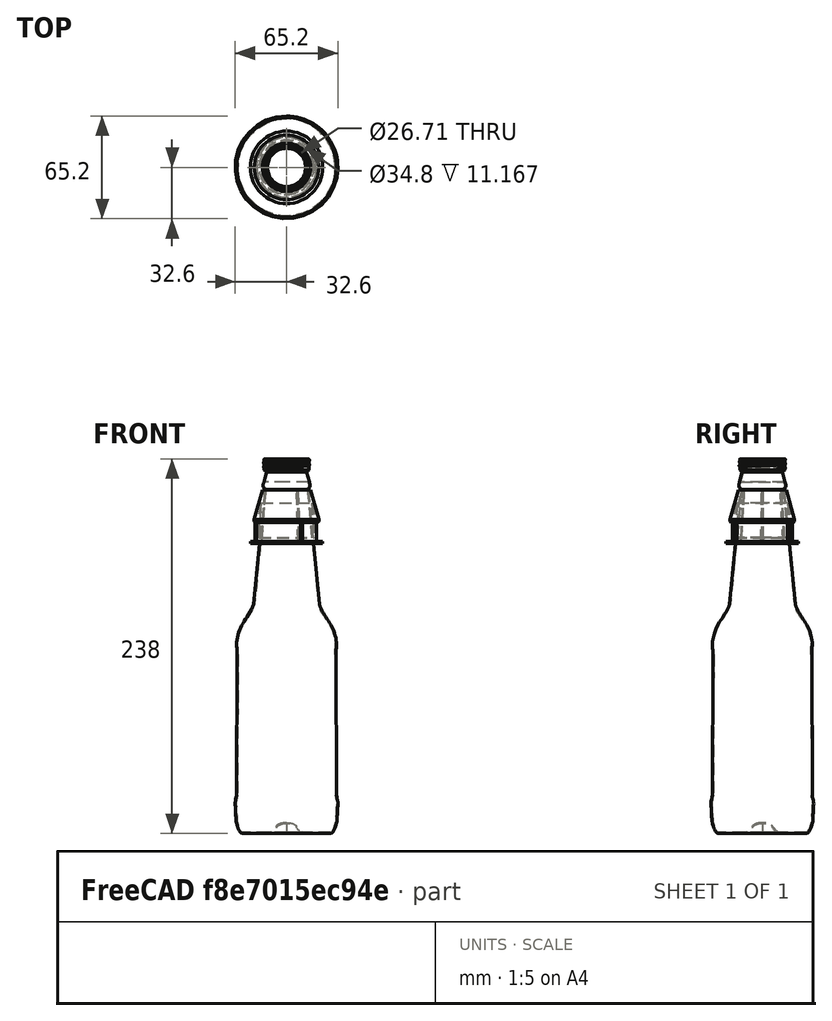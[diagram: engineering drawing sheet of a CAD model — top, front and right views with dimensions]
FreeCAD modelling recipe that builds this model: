
FCSTD DOCUMENT  (FreeCAD 1.0R39319 (Git))
Label: beer_bottle_mount
License: CERN Open Hardware Licence permissive
LicenseURL: https://cern-ohl.web.cern.ch/
objects: Sketcher::SketchObject×3, PartDesign::Pad×2, PartDesign::PolarPattern×2, PartDesign::Revolution×1, Part::Feature×1, Part::Scale×1, Part::FeaturePython×1, PartDesign::Body×1
note: 23 computed .brp shape members not serialized (recipe doc carries the construction recipe); baked Part::Feature solids carry a one-line shape summary decoded from their .brp

FEATURE [Sketcher::SketchObject] Sketch
  ArcFitTolerance = 1e-06
  AttachmentSupport = -> [XZ_Plane]
  FullyConstrained = true
  MakeInternals = false
  MapMode = 5
  Placement = pos=(0,0,0) rot=(1,0,0;1.5708rad)
  expr: Constraints[14] = 32 / 2
  expr: Constraints[15] = 27.5 / 2
  expr: Constraints[17] = 38 / 2
  expr: Constraints[21] = 46 / 2
  sketch-geometry (22):
    g0: LineSegment StartX=-23 StartY=1.5 StartZ=0 EndX=-23 EndY=0 EndZ=0
    g1: LineSegment StartX=-23 StartY=0 StartZ=0 EndX=-17 EndY=0 EndZ=0
    g2: LineSegment StartX=-16 StartY=1 StartZ=0 EndX=-13.75 EndY=34 EndZ=0
    g3: LineSegment StartX=-13.75 StartY=34 StartZ=0 EndX=-15.25 EndY=34 EndZ=0
    g4: LineSegment StartX=-15.25 StartY=34 StartZ=0 EndX=-20.5 EndY=15.2 EndZ=0
    g5: LineSegment StartX=-20.5 StartY=15.2 StartZ=0 EndX=-20.5 EndY=14.2 EndZ=0
    g6: LineSegment StartX=-20.5 StartY=14.2 StartZ=0 EndX=-19.8 EndY=13.5 EndZ=0
    g7: LineSegment StartX=-19.8 StartY=13.5 StartZ=0 EndX=-19 EndY=13.5 EndZ=0
    g8: LineSegment StartX=-19 StartY=13.5 StartZ=0 EndX=-19 EndY=1.5 EndZ=0
    g9: LineSegment StartX=-19 StartY=1.5 StartZ=0 EndX=-23 EndY=1.5 EndZ=0
    g10: LineSegment StartX=-16 StartY=1 StartZ=0 EndX=-17 EndY=0 EndZ=0
    g11: LineSegment StartX=-15.9189 StartY=25.6559 StartZ=0 EndX=-18.8667 EndY=15.1 EndZ=0
    g12: LineSegment StartX=-18.8667 StartY=15.1 StartZ=0 EndX=-17.4 EndY=15.1 EndZ=0
    g13: LineSegment StartX=-17.4 StartY=15.1 StartZ=0 EndX=-17.4 EndY=3.5 EndZ=0
    g14: LineSegment [constr] StartX=-15.9189 StartY=25.6559 StartZ=0 EndX=-17.46 EndY=26.0863 EndZ=0
    g15: LineSegment [constr] StartX=-15.9189 StartY=25.6559 StartZ=0 EndX=-14.3189 EndY=25.6559 EndZ=0
    g16: LineSegment [constr] StartX=-20.5 StartY=15.1 StartZ=0 EndX=-18.9 EndY=15.1 EndZ=0
    g17: LineSegment StartX=-17.4 StartY=3.5 StartZ=0 EndX=-17.4295 EndY=3.5 EndZ=0
    g18: LineSegment StartX=-17.4295 StartY=3.5 StartZ=0 EndX=-15.9189 EndY=25.6559 EndZ=0
    g19: LineSegment [constr] StartX=-17.4 StartY=3.5 StartZ=0 EndX=-19 EndY=3.5 EndZ=0
    g20: LineSegment [constr] StartX=-17.4295 StartY=3.5 StartZ=0 EndX=-15.8295 EndY=3.5 EndZ=0
    g21: LineSegment [constr] StartX=-18.9 StartY=15.1 StartZ=0 EndX=-18.9 EndY=13.5 EndZ=0
  constraints (68):
    c: Vertical(g0)
    c: Coincident(g0,g1)
    c: Horizontal(g1)
    c: Coincident(g2,g3)
    c: Horizontal(g3)
    c: Coincident(g3,g4)
    c: Coincident(g4,g5)
    c: Coincident(g5,g6)
    c: Coincident(g6,g7)
    c: Horizontal(g7)
    c: Coincident(g7,g8)
    c: Vertical(g8)
    c: Coincident(g8,g9)
    c: Coincident(g9,g0)
    c: Distance(g2,g-2) = 16
    c: Distance(g2,g-2) = 13.75
    c: DistanceX(g3,g3) = 1.5
    c: Distance(g7,g-2) = 19
    c: PointOnObject(g1,g-1)
    c: Horizontal(g9)
    c: Distance(g0,g0) = 1.5
    c: DistanceX(g0,g-1) = 23
    c: Angle(g7,g6) = 2.35619
    c: DistanceY(g5,g5) = 1
    c: Coincident(g10,g2)
    c: Coincident(g10,g1)
    c: Angle(g10,g1) = 2.35619
    c: DistanceX(g10,g10) = 1
    c: DistanceY(g8,g8) = 12
    c: DistanceX(g7,g7) = 0.8
    c: Vertical(g5)
    c: DistanceX(g4,g-1) = 20.5
    c: Distance(g2,g-1) = 34
    c: Coincident(g18,g11)
    c: Coincident(g12,g13)
    c: Parallel(g13,g8)
    c: Parallel(g12,g7)
    c: Parallel(g11,g4)
    c: Coincident(g14,g18)
    c: PointOnObject(g14,g4)
    c: Coincident(g15,g18)
    c: PointOnObject(g15,g2)
    c: Horizontal(g15)
    c: Equal(g14,g15)
    c: Perpendicular(g4,g14)
    c: Distance(g15,g15) = 1.6
    c: PointOnObject(g16,g5)
    c: Horizontal(g16)
    c: Equal(g16,g15)
    c: Horizontal(g17)
    c: PointOnObject(g17,g18)
    c: PointOnObject(g18,g17)
    c: Coincident(g13,g17)
    c: Coincident(g19,g13)
    c: PointOnObject(g19,g8)
    c: Horizontal(g19)
    c: Coincident(g20,g17)
    c: PointOnObject(g20,g2)
    c: Horizontal(g20)
    c: Equal(g19,g20)
    c: Equal(g20,g15)
    c: Distance(g19,g8) = 2
    c: Vertical(g21)
    c: PointOnObject(g21,g7)
    c: Equal(g21,g16)
    c: Coincident(g11,g12)
    c: Coincident(g21,g16)
    c: Horizontal(g11,g16)
FEATURE [PartDesign::Revolution] Revolution
  Angle = 360
  Angle2 = 60
  Axis = (0,2e-16,1)
  Base = (0,0,0)
  Placement = pos=(0,0,0) rot=(1,0,0;1.5708rad)
  Profile = -> Sketch
  ReferenceAxis = -> Sketch [V_Axis]
  Refine = true
  Suppressed = false
  Type = 0
FEATURE [Sketcher::SketchObject] Sketch001
  ArcFitTolerance = 1e-06
  AttachmentSupport = -> [XZ_Plane]
  ExternalGeometry = -> [Revolution]
  FullyConstrained = true
  MakeInternals = false
  MapMode = 5
  Placement = pos=(0,0,0) rot=(1,0,0;1.5708rad)
  sketch-geometry (4):
    g0: LineSegment StartX=-13.75 StartY=34 StartZ=0 EndX=-16 EndY=1 EndZ=0
    g1: LineSegment StartX=-16 StartY=1 StartZ=0 EndX=-15.5 EndY=1.43617 EndZ=0
    g2: LineSegment StartX=-15.5 StartY=1.43617 StartZ=0 EndX=-13.3138 EndY=33.5 EndZ=0
    g3: LineSegment StartX=-13.3138 StartY=33.5 StartZ=0 EndX=-13.75 EndY=34 EndZ=0
  constraints (10):
    c: Coincident(g0,g1)
    c: Coincident(g1,g2)
    c: Coincident(g2,g3)
    c: Coincident(g3,g0)
    c: Parallel(g2,g0)
    c: Angle(g0,g3) = 0.785398
    c: Angle(g1,g0) = 0.785398
    c: Coincident(g0,g-3)
    c: Coincident(g0,g-3)
    c: DistanceX(g0,g1) = 0.5
FEATURE [PartDesign::Pad] Pad
  BaseFeature = -> Revolution
  Direction = (0,-1,2e-16)
  Length = 1
  Length2 = 10
  Midplane = true
  Placement = pos=(0,0,0) rot=(1,0,0;1.5708rad)
  Profile = -> Sketch001
  ReferenceAxis = -> Sketch001 [N_Axis]
  Refine = true
  Suppressed = false
  Type = 0
FEATURE [Part::Feature] Part__Feature  label="Part 1 v1"
  Placement = pos=(0,-1.07e-13,-481.9) rot=(1,0,0;1.5708rad)
  shape: bbox 130.6 x 130.6 x 477 mm, 50 faces (baked)
FEATURE [Part::Scale] Scale
  Base = -> Part__Feature
  Placement = pos=(0,-1.065e-13,-424.5) rot=(1,0,0;1.5708rad)
  Uniform = true
  UniformScale = 0.5
  XScale = 1
  YScale = 1
  ZScale = 1
FEATURE [Part::FeaturePython] LinearArray  # WARN: FeaturePython — macro-defined, semantics opaque (R4)
  Alignment = 0
  CellStart = A1
  Count = 25
  Dir = (1,0,0)
  DirIsDriven = true
  DistributionLaw = 0
  DrivenProperty = 1
  EndInclusive = true
  ExposePlacement = false
  GeneratorMode = 1
  MarkerShape = 1
  MarkerSize = 0
  NumElements = 25
  OrientMode = 1
  Point = (0,0,0)
  PointIsDriven = true
  Reverse = false
  SpanEnd = 1625
  SpanStart = 0
  Step = 65
  Type = lattice2LinearArray.LinearArray
  VSGVersion = 1
  Values = 0.0 | 65.0 | 130.0 | 195.0 | 260.0 | 325.0 | 390.0 | 455.0 | 520.0 | 585.0 | 650.0 | 715.0 | 780.0 | 845.0 | 910.0 | 975.0 | 1040.0 | 1105.0 | 1170.0 | 1235.0 | 1300.0 | 1365.0 | 1430.0 | 1495.0 | 1560.0
  ValuesSource = 2
  isLattice = 1
FEATURE [PartDesign::PolarPattern] PolarPattern
  Angle = 360
  Axis = -> Z_Axis
  BaseFeature = -> Pad
  Mode = 0
  Occurrences = 3
  Offset = 120
  Originals = -> [Pad]
  Placement = pos=(0,0,0) rot=(1,0,0;1.5708rad)
  Refine = true
  Suppressed = false
  TransformMode = 0
FEATURE [Sketcher::SketchObject] Sketch002
  ArcFitTolerance = 1e-06
  AttachmentSupport = -> [PolarPattern]
  ExternalGeometry = -> [PolarPattern]
  FullyConstrained = true
  MakeInternals = false
  MapMode = 5
  Placement = pos=(0,7e-16,1.5) rot=(0,0,1;3.14159rad)
  sketch-geometry (5):
    g0: LineSegment StartX=18.9852 StartY=0.75 StartZ=0 EndX=18.9852 EndY=-0.75 EndZ=0
    g1: LineSegment StartX=18.9852 StartY=-0.75 StartZ=0 EndX=19.6842 EndY=-0.34641 EndZ=0
    g2: ArcOfCircle CenterX=19.4842 CenterY=4e-16 CenterZ=0 NormalX=0 NormalY=0 NormalZ=1 AngleXU=0 Radius=0.4 StartAngle=5.23599 EndAngle=7.33038
    g3: LineSegment StartX=19.6842 StartY=0.34641 StartZ=0 EndX=18.9852 EndY=0.75 EndZ=0
    g4: LineSegment [constr] StartX=18.9852 StartY=0 StartZ=0 EndX=19.8842 EndY=0 EndZ=0
  constraints (14):
    c: Coincident(g0,g1)
    c: Tangent(g1,g2) = -1.5708
    c: Coincident(g3,g0)
    c: Tangent(g2,g3) = -1.5708
    c: Radius(g2) = 0.4
    c: Angle(g1,g0) = 1.0472
    c: Angle(g0,g3) = 1.0472
    c: Symmetric(g0,g0,g4)
    c: Perpendicular(g0,g4)
    c: PointOnObject(g4,g2)
    c: Distance(g0) = 1.5
    c: PointOnObject(g4,g-1)
    c: PointOnObject(g4,g-1)
    c: PointOnObject(g0,g-3)
FEATURE [PartDesign::Pad] Pad001
  BaseFeature = -> PolarPattern
  Direction = (0,0,1)
  Length = 10
  Length2 = 10
  Placement = pos=(0,0,0) rot=(1,0,0;1.5708rad)
  Profile = -> Sketch002
  ReferenceAxis = -> Sketch002 [N_Axis]
  Refine = true
  Suppressed = false
  Type = 3
  UpToFace = -> PolarPattern [Face28]
FEATURE [PartDesign::PolarPattern] PolarPattern001
  Angle = 360
  Axis = -> Z_Axis
  BaseFeature = -> Pad001
  Mode = 0
  Occurrences = 3
  Offset = 120
  Originals = -> [Pad001]
  Placement = pos=(0,0,0) rot=(1,0,0;1.5708rad)
  Refine = true
  Suppressed = false
  TransformMode = 0
FEATURE [PartDesign::Body] Body
  AllowCompound = false
  Group = -> [Sketch,Revolution,Sketch001,Pad,Sketch002,PolarPattern,Pad001,PolarPattern001]
  Origin = -> Origin
  Tip = -> PolarPattern001
